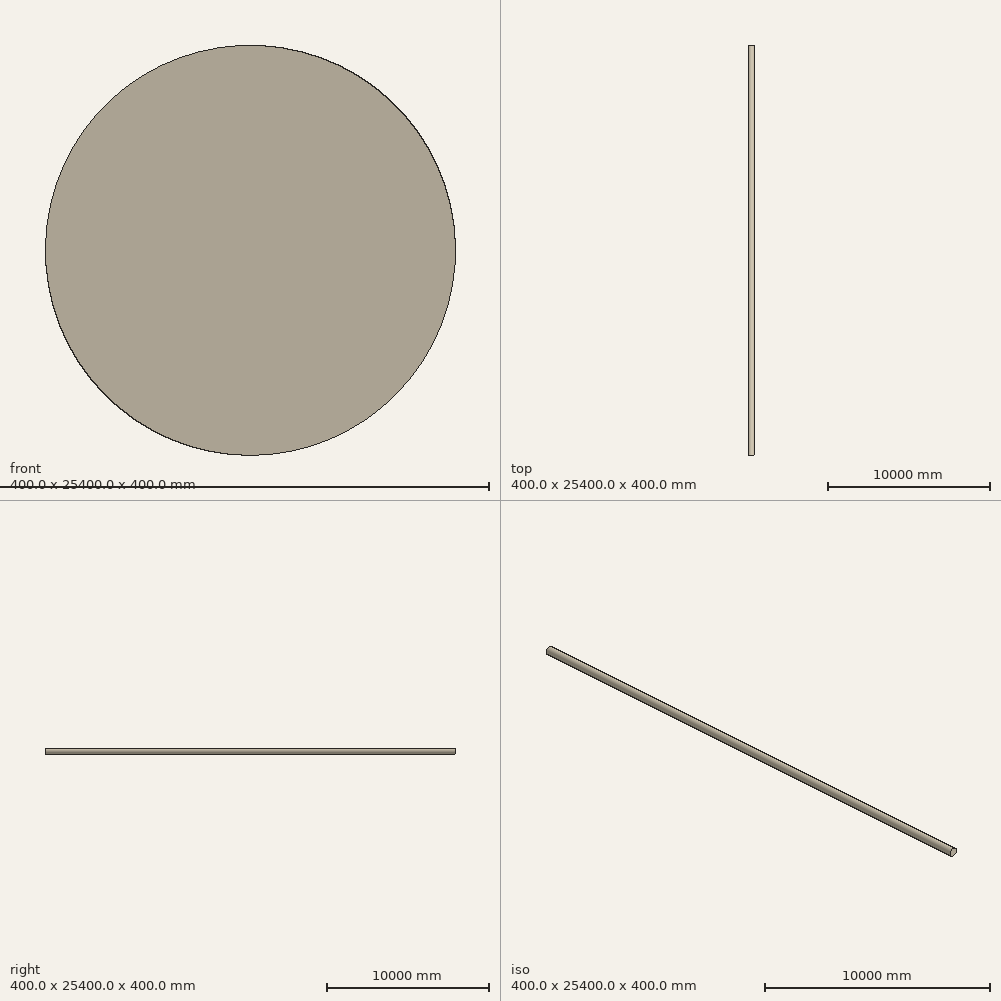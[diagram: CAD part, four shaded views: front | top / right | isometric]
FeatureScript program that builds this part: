
annotation { "Feature Type Name" : "Feature", "Feature Type Description" : "" }
export const myFeature = defineFeature(function(context is Context, id is Id, definition is map)
    precondition{}
    {
        {
            var Q0;
            Q0=qCreatedBy(makeId("Front.planeOp"),FACE);
            var sketch = newSketch(context, id + "F0", { "sketchPlane" : qUnion([Q0])});
            skCircle(sketch, "E0", {"center": v(0, 0) * mm, "radius": 200 * mm});
            skSolve(sketch);
        }
        {
            var Q0;
            Q0 = qSketchRegion(id + "F0", true);
            extrude(context, id + "F1", {"entities" : qUnion([Q0]), "depth" : 25400 * mm, "offsetDistance" : 25.4 * mm});
        }
    });
